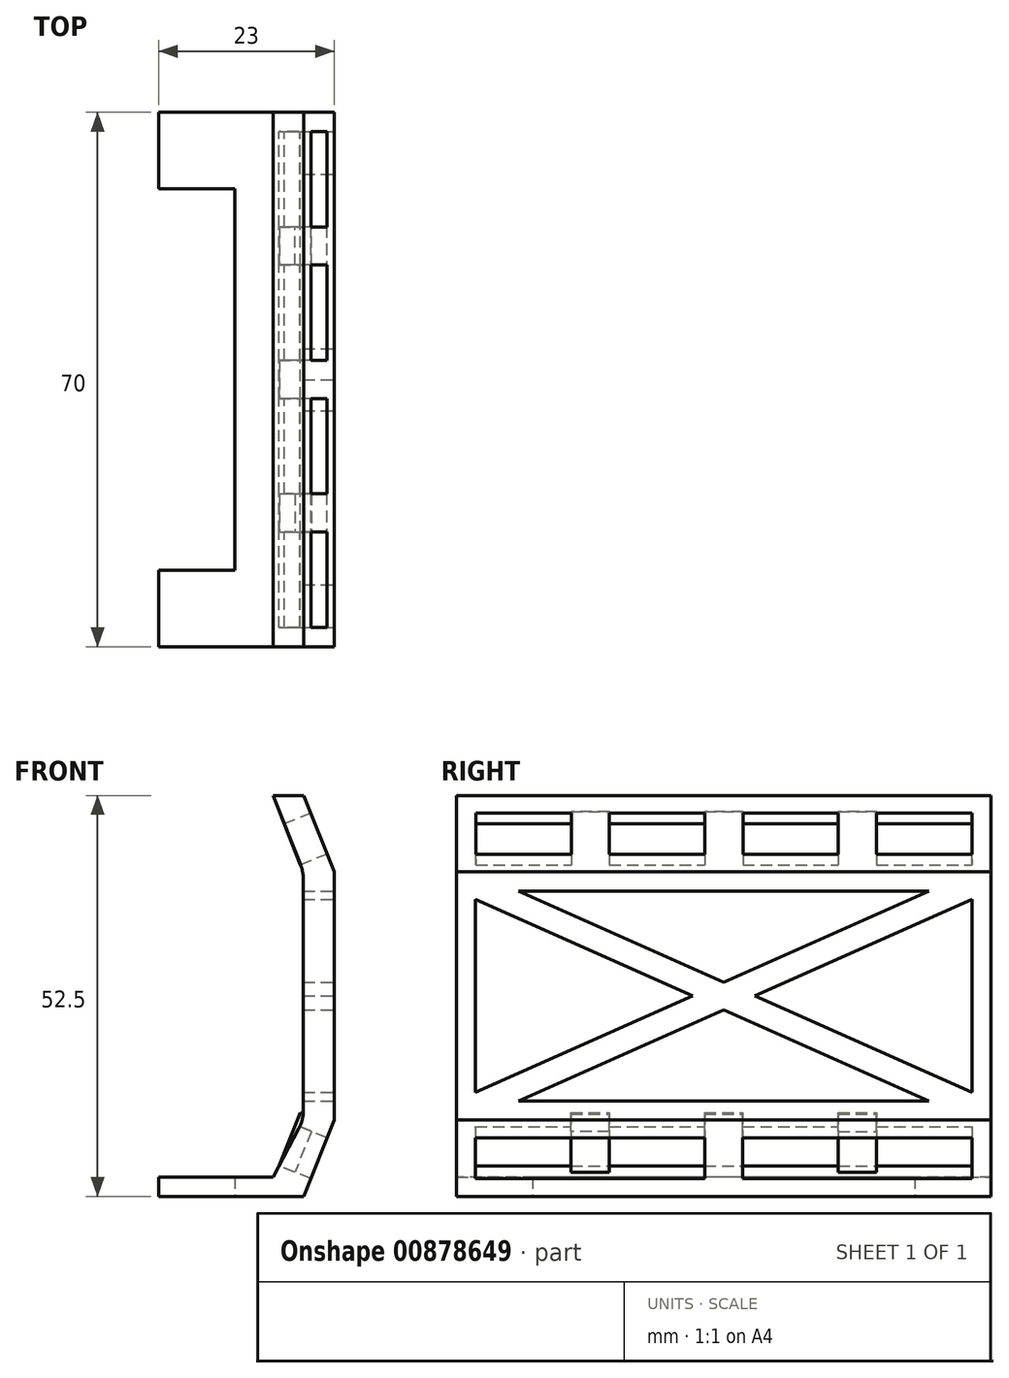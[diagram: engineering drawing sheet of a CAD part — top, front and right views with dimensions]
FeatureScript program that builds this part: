
annotation { "Feature Type Name" : "Feature", "Feature Type Description" : "" }
export const myFeature = defineFeature(function(context is Context, id is Id, definition is map)
    precondition{}
    {
        {
            var Q0;
            Q0=qCreatedBy(makeId("Top.planeOp"),FACE);
            var sketch = newSketch(context, id + "F0", { "sketchPlane" : qUnion([Q0])});
            skLineSegment(sketch, "E0.bottom", {"start": v(10, -35) * mm, "end": v(-10, -35) * mm});
            skLineSegment(sketch, "E0.top", {"start": v(10, 35) * mm, "end": v(-10, 35) * mm});
            skLineSegment(sketch, "E0.left", {"start": v(10, -35) * mm, "end": v(10, 35) * mm});
            skLineSegment(sketch, "E0.right", {"start": v(-10, -35) * mm, "end": v(-10, 35) * mm});
            skPoint(sketch, "E0.middle", {"position": v(0, 0) * mm});
            skLineSegment(sketch, "E1", {"start": v(-10, -35) * mm, "end": v(-10, -25) * mm});
            skLineSegment(sketch, "E2", {"start": v(-10, 35) * mm, "end": v(-10, 25) * mm});
            skLineSegment(sketch, "E3.bottom", {"start": v(-10, 25) * mm, "end": v(0, 25) * mm});
            skLineSegment(sketch, "E3.top", {"start": v(-10, -25) * mm, "end": v(0, -25) * mm});
            skLineSegment(sketch, "E3.left", {"start": v(-10, 25) * mm, "end": v(-10, -25) * mm});
            skLineSegment(sketch, "E3.right", {"start": v(0, 25) * mm, "end": v(0, -25) * mm});
            skSolve(sketch);
        }
        {
            var Q0;
            Q0=makeQuery(id+"F0.imprint","IMPRINT",FACE,{"disambiguationData":[TD([[makeQuery(id+"F0.imprint","IMPRINT",EDGE,{"derivedFrom":sQuery(id+"F0.wireOp",EDGE,"E0.bottom")}),-1.0]])]});
            extrude(context, id + "F1", {"entities" : qUnion([Q0]), "depth" : 2.5 * mm, "offsetDistance" : 25 * mm});
        }
        {
            var Q0;
            Q0=makeQuery(id+"F1.opExtrude","CAP_FACE",FACE,{"disambiguationData":[OSD([sQuery(id+"F0.wireOp",EDGE,"E0.bottom"),sQuery(id+"F0.wireOp",EDGE,"E0.top"),sQuery(id+"F0.wireOp",EDGE,"E0.left"),sQuery(id+"F0.wireOp",EDGE,"E1"),sQuery(id+"F0.wireOp",EDGE,"E2"),sQuery(id+"F0.wireOp",EDGE,"E3.bottom"),sQuery(id+"F0.wireOp",EDGE,"E3.top"),sQuery(id+"F0.wireOp",EDGE,"E3.right")])],"isStart":false});
            var sketch = newSketch(context, id + "F2", { "sketchPlane" : qUnion([Q0])});
            skLineSegment(sketch, "E4.bottom", {"start": v(10, 35) * mm, "end": v(5, 35) * mm});
            skLineSegment(sketch, "E4.top", {"start": v(10, -35) * mm, "end": v(5, -35) * mm});
            skLineSegment(sketch, "E4.left", {"start": v(10, 35) * mm, "end": v(10, -35) * mm});
            skLineSegment(sketch, "E4.right", {"start": v(5, 35) * mm, "end": v(5, -35) * mm});
            skSolve(sketch);
        }
        {
            var Q0;
            Q0=makeQuery(id+"F2.imprint","IMPRINT",FACE,{"disambiguationData":[TD([[makeQuery(id+"F2.imprint","IMPRINT",EDGE,{"derivedFrom":sQuery(id+"F2.wireOp",EDGE,"E4.bottom")}),1.0]])]});
            extrude(context, id + "F3", {"entities" : qUnion([Q0]), "operationType" : NewBodyOperationType.ADD, "depth" : 50 * mm, "offsetDistance" : 25 * mm});
        }
        {
            var Q0;
            Q0=makeQuery(id+"F3.boolean.opBoolean","MERGE",FACE,{"derivedFrom":[makeQuery(id+"F1.opExtrude","SWEPT_FACE",FACE,{"disambiguationData":[OSD([sQuery(id+"F0.wireOp",EDGE,"E0.left")])]}),makeQuery(id+"F3.opExtrude","SWEPT_FACE",FACE,{"disambiguationData":[OSD([sQuery(id+"F2.wireOp",EDGE,"E4.left")])]})]});
            extrude(context, id + "F4", {"entities" : qUnion([Q0]), "operationType" : NewBodyOperationType.ADD, "depth" : 3 * mm, "offsetDistance" : 25 * mm});
        }
        {
            var Q0;
            {var subQ0=sQuery(id+"F2.wireOp",EDGE,"E4.top");var subQ1=sQuery(id+"F0.wireOp",EDGE,"E0.bottom");Q0=makeQuery(id+"F4.boolean.opBoolean","MERGE",FACE,{"derivedFrom":[makeQuery(id+"F3.boolean.opBoolean","MERGE",FACE,{"derivedFrom":[makeQuery(id+"F1.opExtrude","SWEPT_FACE",FACE,{"disambiguationData":[OSD([subQ1])]}),makeQuery(id+"F3.opExtrude","SWEPT_FACE",FACE,{"disambiguationData":[OSD([subQ0])]})]}),makeQuery(id+"F4.opExtrude","SWEPT_FACE",FACE,{"disambiguationData":[OSD([subQ1,sQuery(id+"F0.wireOp",EDGE,"E0.left"),subQ0,sQuery(id+"F2.wireOp",EDGE,"E4.left")])]})]});}
            var sketch = newSketch(context, id + "F5", { "sketchPlane" : qUnion([Q0])});
            skLineSegment(sketch, "E5", {"start": v(13, 52.5) * mm, "end": v(13, 42.5) * mm});
            skLineSegment(sketch, "E6", {"start": v(13, 0) * mm, "end": v(13, 10) * mm});
            skLineSegment(sketch, "E7", {"start": v(13, 42.5) * mm, "end": v(9, 52.5) * mm});
            skLineSegment(sketch, "E8", {"start": v(13, 10) * mm, "end": v(9, 0) * mm});
            skLineSegment(sketch, "E9", {"start": v(5, 2.5) * mm, "end": v(8.95, 10) * mm});
            skLineSegment(sketch, "E10", {"start": v(8.95, 10) * mm, "end": v(8.95, 42.5) * mm});
            skLineSegment(sketch, "E11", {"start": v(8.95, 42.5) * mm, "end": v(5, 52.5) * mm});
            skSolve(sketch);
        }
        {
            var Q0;
            {var subQ0=sQuery(id+"F5.wireOp",EDGE,"E6");Q0=makeQuery(id+"F5.imprint","IMPRINT",FACE,{"disambiguationData":[TD([[makeQuery(id+"F5.imprint","IMPRINT",EDGE,{"derivedFrom":subQ0}),-1.0]])]});}
            var Q1;
            Q1=makeQuery(id+"F5.imprint","IMPRINT",FACE,{"disambiguationData":[TD([[makeQuery(id+"F5.imprint","IMPRINT",EDGE,{"derivedFrom":sQuery(id+"F5.wireOp",EDGE,"E9")}),1.0]])]});
            var Q2;
            {var subQ0=sQuery(id+"F5.wireOp",EDGE,"E5");Q2=makeQuery(id+"F5.imprint","IMPRINT",FACE,{"disambiguationData":[TD([[makeQuery(id+"F5.imprint","IMPRINT",EDGE,{"derivedFrom":subQ0}),-1.0]])]});}
            extrude(context, id + "F6", {"entities" : qUnion([Q0, Q1, Q2]), "operationType" : NewBodyOperationType.REMOVE, "oppositeDirection" : true, "depth" : 70 * mm, "offsetDistance" : 25 * mm});
        }
        {
            var Q0;
            Q0=makeQuery(id+"F6.boolean.opBoolean","COPY",FACE,{"derivedFrom":makeQuery(id+"F6.opExtrude","SWEPT_FACE",FACE,{"disambiguationData":[OSD([sQuery(id+"F5.wireOp",EDGE,"E7")])]})});
            var sketch = newSketch(context, id + "F7", { "sketchPlane" : qUnion([Q0])});
            skLineSegment(sketch, "E12.bottom", {"start": v(-32.45, 42.9) * mm, "end": v(32.5, 42.9) * mm});
            skLineSegment(sketch, "E12.top", {"start": v(-32.45, 37.13) * mm, "end": v(32.5, 37.13) * mm});
            skLineSegment(sketch, "E12.left", {"start": v(-32.45, 42.9) * mm, "end": v(-32.45, 37.13) * mm});
            skLineSegment(sketch, "E12.right", {"start": v(32.5, 42.9) * mm, "end": v(32.5, 37.13) * mm});
            skPoint(sketch, "E13.end.orphan", {"position": v(35, 37.13) * mm});
            skPoint(sketch, "E14.end.orphan", {"position": v(-32.45, 45.4) * mm});
            skSolve(sketch);
        }
        {
            var Q0;
            Q0=makeQuery(id+"F7.imprint","IMPRINT",FACE,{"disambiguationData":[TD([[makeQuery(id+"F7.imprint","IMPRINT",EDGE,{"derivedFrom":sQuery(id+"F7.wireOp",EDGE,"E12.bottom")}),-1.0]])]});
            extrude(context, id + "F8", {"entities" : qUnion([Q0]), "operationType" : NewBodyOperationType.REMOVE, "oppositeDirection" : true, "depth" : 25 * mm, "offsetDistance" : 25 * mm});
        }
        {
            var Q0;
            Q0=makeQuery(id+"F4.opExtrude","CAP_FACE",FACE,{"disambiguationData":[OSD([sQuery(id+"F0.wireOp",EDGE,"E0.left"),sQuery(id+"F2.wireOp",EDGE,"E4.left")])],"isStart":false});
            var sketch = newSketch(context, id + "F9", { "sketchPlane" : qUnion([Q0])});
            skLineSegment(sketch, "E15", {"start": v(35, 10) * mm, "end": v(35, 12.5) * mm});
            skLineSegment(sketch, "E16", {"start": v(35, 10) * mm, "end": v(32.5, 10) * mm});
            skLineSegment(sketch, "E17", {"start": v(32.5, 10) * mm, "end": v(32.5, 12.5) * mm});
            skLineSegment(sketch, "E18", {"start": v(32.5, 12.5) * mm, "end": v(35, 12.5) * mm});
            skLineSegment(sketch, "E19", {"start": v(-32.5, 42.5) * mm, "end": v(-32.5, 40) * mm});
            skLineSegment(sketch, "E20", {"start": v(-32.5, 40) * mm, "end": v(-35, 40) * mm});
            skLineSegment(sketch, "E21.bottom", {"start": v(32.5, 12.5) * mm, "end": v(-32.5, 12.5) * mm});
            skLineSegment(sketch, "E21.top", {"start": v(32.5, 40) * mm, "end": v(-32.5, 40) * mm});
            skLineSegment(sketch, "E21.left", {"start": v(32.5, 12.5) * mm, "end": v(32.5, 40) * mm});
            skLineSegment(sketch, "E21.right", {"start": v(-32.5, 12.5) * mm, "end": v(-32.5, 40) * mm});
            skLineSegment(sketch, "E22", {"start": v(-32.5, 42.5) * mm, "end": v(35, 12.5) * mm});
            skLineSegment(sketch, "E23", {"start": v(32.5, 10) * mm, "end": v(-35, 40) * mm});
            skLineSegment(sketch, "E24.bottom", {"start": v(32.5, 40) * mm, "end": v(35, 40) * mm});
            skLineSegment(sketch, "E24.top", {"start": v(32.5, 42.5) * mm, "end": v(35, 42.5) * mm});
            skLineSegment(sketch, "E24.left", {"start": v(32.5, 40) * mm, "end": v(32.5, 42.5) * mm});
            skLineSegment(sketch, "E24.right", {"start": v(35, 40) * mm, "end": v(35, 42.5) * mm});
            skLineSegment(sketch, "E25.bottom", {"start": v(-32.5, 12.5) * mm, "end": v(-35, 12.5) * mm});
            skLineSegment(sketch, "E25.top", {"start": v(-32.5, 10) * mm, "end": v(-35, 10) * mm});
            skLineSegment(sketch, "E25.left", {"start": v(-32.5, 12.5) * mm, "end": v(-32.5, 10) * mm});
            skLineSegment(sketch, "E25.right", {"start": v(-35, 12.5) * mm, "end": v(-35, 10) * mm});
            skLineSegment(sketch, "E26", {"start": v(-35, 12.5) * mm, "end": v(32.5, 42.5) * mm});
            skLineSegment(sketch, "E27", {"start": v(-32.5, 10) * mm, "end": v(35, 40) * mm});
            skSolve(sketch);
        }
        {
            var Q0;
            Q0=makeQuery(id+"F9.imprint","IMPRINT",FACE,{"disambiguationData":[TD([[makeQuery(id+"F9.imprint","IMPRINT",EDGE,{"derivedFrom":sQuery(id+"F9.wireOp",EDGE,"E21.bottom")}),-1.0]])]});
            var Q1;
            {var subQ0=sQuery(id+"F9.wireOp",EDGE,"E26");var subQ1=sQuery(id+"F9.wireOp",EDGE,"E21.right");var subQ2=makeQuery(id+"F9.imprint","INTERSECT",VERTEX,{"derivedFrom":[subQ1,subQ0]});Q1=makeQuery(id+"F9.imprint","IMPRINT",FACE,{"disambiguationData":[TD([[makeQuery(id+"F9.imprint","IMPRINT",EDGE,{"disambiguationData":[TD([[subQ2,-1.0]])],"derivedFrom":subQ1}),-1.0]])]});}
            var Q2;
            {var subQ0=sQuery(id+"F9.wireOp",EDGE,"E26");var subQ1=sQuery(id+"F9.wireOp",EDGE,"E21.top");var subQ2=makeQuery(id+"F9.imprint","INTERSECT",VERTEX,{"derivedFrom":[subQ1,subQ0]});Q2=makeQuery(id+"F9.imprint","IMPRINT",FACE,{"disambiguationData":[TD([[makeQuery(id+"F9.imprint","IMPRINT",EDGE,{"disambiguationData":[TD([[subQ2,-1.0]])],"derivedFrom":subQ1}),1.0]])]});}
            var Q3;
            {var subQ0=sQuery(id+"F9.wireOp",EDGE,"E22");var subQ1=sQuery(id+"F9.wireOp",EDGE,"E21.left");var subQ2=makeQuery(id+"F9.imprint","INTERSECT",VERTEX,{"derivedFrom":[subQ1,subQ0]});Q3=makeQuery(id+"F9.imprint","IMPRINT",FACE,{"disambiguationData":[TD([[makeQuery(id+"F9.imprint","IMPRINT",EDGE,{"disambiguationData":[TD([[subQ2,-1.0]])],"derivedFrom":subQ1}),1.0]])]});}
            extrude(context, id + "F10", {"entities" : qUnion([Q0, Q1, Q2, Q3]), "operationType" : NewBodyOperationType.REMOVE, "oppositeDirection" : true, "depth" : 25 * mm, "offsetDistance" : 25 * mm});
        }
        {
            var Q0;
            Q0=makeQuery(id+"F6.boolean.opBoolean","COPY",FACE,{"derivedFrom":makeQuery(id+"F6.opExtrude","SWEPT_FACE",FACE,{"disambiguationData":[OSD([sQuery(id+"F5.wireOp",EDGE,"E8")])]})});
            var sketch = newSketch(context, id + "F11", { "sketchPlane" : qUnion([Q0])});
            skLineSegment(sketch, "E28", {"start": v(-32.5, 14.11) * mm, "end": v(-32.5, 11.61) * mm});
            skLineSegment(sketch, "E29", {"start": v(-32.5, 11.61) * mm, "end": v(-35, 11.61) * mm});
            skLineSegment(sketch, "E30", {"start": v(35, 5.84) * mm, "end": v(32.5, 5.84) * mm});
            skLineSegment(sketch, "E31", {"start": v(32.5, 5.84) * mm, "end": v(32.5, 3.34) * mm});
            skLineSegment(sketch, "E32.bottom", {"start": v(-32.5, 11.61) * mm, "end": v(32.5, 11.61) * mm});
            skLineSegment(sketch, "E32.top", {"start": v(-32.5, 5.84) * mm, "end": v(32.5, 5.84) * mm});
            skLineSegment(sketch, "E32.left", {"start": v(-32.5, 11.61) * mm, "end": v(-32.5, 5.84) * mm});
            skLineSegment(sketch, "E32.right", {"start": v(32.5, 11.61) * mm, "end": v(32.5, 5.84) * mm});
            skSolve(sketch);
        }
        {
            var Q0;
            Q0=makeQuery(id+"F11.imprint","IMPRINT",FACE,{"disambiguationData":[TD([[makeQuery(id+"F11.imprint","IMPRINT",EDGE,{"derivedFrom":sQuery(id+"F11.wireOp",EDGE,"E32.bottom")}),-1.0]])]});
            extrude(context, id + "F12", {"entities" : qUnion([Q0]), "operationType" : NewBodyOperationType.REMOVE, "oppositeDirection" : true, "depth" : 25 * mm, "offsetDistance" : 25 * mm});
        }
        {
            var Q0;
            Q0=makeQuery(id+"F6.boolean.opBoolean","COPY",EDGE,{"derivedFrom":makeQuery(id+"F6.opExtrude","SWEPT_EDGE",EDGE,{"disambiguationData":[OSD([sQuery(id+"F0.wireOp",EDGE,"E0.bottom"),sQuery(id+"F0.wireOp",EDGE,"E0.left"),sQuery(id+"F2.wireOp",EDGE,"E4.top"),sQuery(id+"F2.wireOp",EDGE,"E4.left"),sQuery(id+"F5.wireOp",EDGE,"E6"),sQuery(id+"F5.wireOp",EDGE,"E8")])]})});
            var Q1;
            Q1=makeQuery(id+"F6.boolean.opBoolean","COPY",EDGE,{"derivedFrom":makeQuery(id+"F6.opExtrude","SWEPT_EDGE",EDGE,{"disambiguationData":[OSD([sQuery(id+"F0.wireOp",EDGE,"E0.bottom"),sQuery(id+"F0.wireOp",EDGE,"E0.left"),sQuery(id+"F2.wireOp",EDGE,"E4.top"),sQuery(id+"F2.wireOp",EDGE,"E4.left"),sQuery(id+"F5.wireOp",EDGE,"E5"),sQuery(id+"F5.wireOp",EDGE,"E7")])]})});
            var Q2;
            Q2=makeQuery(id+"F6.boolean.opBoolean","COPY",EDGE,{"derivedFrom":makeQuery(id+"F6.opExtrude","SWEPT_EDGE",EDGE,{"disambiguationData":[OSD([sQuery(id+"F5.wireOp",EDGE,"E9"),sQuery(id+"F5.wireOp",EDGE,"E10")])]})});
            var Q3;
            Q3=makeQuery(id+"F6.boolean.opBoolean","COPY",EDGE,{"derivedFrom":makeQuery(id+"F6.opExtrude","SWEPT_EDGE",EDGE,{"disambiguationData":[OSD([sQuery(id+"F5.wireOp",EDGE,"E10"),sQuery(id+"F5.wireOp",EDGE,"E11")])]})});
            fillet(context, id + "F13", {"entities" : qUnion([Q0, Q1, Q2, Q3]), "radius" : 5 * mm, "tangentPropagation" : true, "allowEdgeOverflow" : false});
        }
        {
            var Q0;
            Q0=makeQuery(id+"F12.boolean.opBoolean","COPY",FACE,{"derivedFrom":makeQuery(id+"F12.opExtrude","SWEPT_FACE",FACE,{"disambiguationData":[OSD([sQuery(id+"F11.wireOp",EDGE,"E32.top")])]})});
            var sketch = newSketch(context, id + "F14", { "sketchPlane" : qUnion([Q0])});
            skLineSegment(sketch, "E33", {"start": v(8.36, -32.5) * mm, "end": v(8.36, 32.5) * mm});
            skLineSegment(sketch, "E34", {"start": v(8.36, 0) * mm, "end": v(3.89, 0) * mm});
            skLineSegment(sketch, "E35", {"start": v(3.89, 0) * mm, "end": v(6.12, 0) * mm});
            skLineSegment(sketch, "E36", {"start": v(6.12, 0) * mm, "end": v(6.12, 2.5) * mm});
            skLineSegment(sketch, "E37", {"start": v(6.12, 0) * mm, "end": v(6.12, -2.5) * mm});
            skLineSegment(sketch, "E38.bottom", {"start": v(8.36, 2.5) * mm, "end": v(3.89, 2.5) * mm});
            skLineSegment(sketch, "E38.top", {"start": v(8.36, -2.5) * mm, "end": v(3.89, -2.5) * mm});
            skLineSegment(sketch, "E38.left", {"start": v(8.36, 2.5) * mm, "end": v(8.36, -2.5) * mm});
            skLineSegment(sketch, "E38.right", {"start": v(3.89, 2.5) * mm, "end": v(3.89, -2.5) * mm});
            skPoint(sketch, "E38.middle", {"position": v(6.12, 0) * mm});
            skLineSegment(sketch, "E39", {"start": v(6.12, 2.5) * mm, "end": v(6.12, 32.5) * mm});
            skLineSegment(sketch, "E40", {"start": v(6.12, -2.5) * mm, "end": v(6.12, -32.5) * mm});
            skLineSegment(sketch, "E41", {"start": v(6.12, -2.5) * mm, "end": v(6.12, -17.5) * mm});
            skLineSegment(sketch, "E42", {"start": v(6.12, -17.5) * mm, "end": v(6.12, 17.5) * mm});
            skLineSegment(sketch, "E43.bottom", {"start": v(8.36, -15) * mm, "end": v(3.89, -15) * mm});
            skLineSegment(sketch, "E43.top", {"start": v(8.36, -20) * mm, "end": v(3.89, -20) * mm});
            skLineSegment(sketch, "E43.left", {"start": v(8.36, -15) * mm, "end": v(8.36, -20) * mm});
            skLineSegment(sketch, "E43.right", {"start": v(3.89, -15) * mm, "end": v(3.89, -20) * mm});
            skPoint(sketch, "E43.middle", {"position": v(6.12, -17.5) * mm});
            skLineSegment(sketch, "E44.bottom", {"start": v(8.36, 20) * mm, "end": v(3.89, 20) * mm});
            skLineSegment(sketch, "E44.top", {"start": v(8.36, 15) * mm, "end": v(3.89, 15) * mm});
            skLineSegment(sketch, "E44.left", {"start": v(8.36, 20) * mm, "end": v(8.36, 15) * mm});
            skLineSegment(sketch, "E44.right", {"start": v(3.89, 20) * mm, "end": v(3.89, 15) * mm});
            skPoint(sketch, "E44.middle", {"position": v(6.12, 17.5) * mm});
            skSolve(sketch);
        }
        {
            var Q0;
            {var subQ0=sQuery(id+"F14.wireOp",EDGE,"E35");Q0=makeQuery(id+"F14.imprint","IMPRINT",FACE,{"disambiguationData":[TD([[makeQuery(id+"F14.imprint","IMPRINT",EDGE,{"derivedFrom":subQ0}),1.0]])]});}
            var Q1;
            {var subQ0=sQuery(id+"F14.wireOp",EDGE,"E35");Q1=makeQuery(id+"F14.imprint","IMPRINT",FACE,{"disambiguationData":[TD([[makeQuery(id+"F14.imprint","IMPRINT",EDGE,{"derivedFrom":subQ0}),-1.0]])]});}
            var Q2;
            {var subQ0=sQuery(id+"F14.wireOp",EDGE,"E34");Q2=makeQuery(id+"F14.imprint","IMPRINT",FACE,{"disambiguationData":[TD([[makeQuery(id+"F14.imprint","IMPRINT",EDGE,{"derivedFrom":subQ0}),1.0]])]});}
            var Q3;
            {var subQ0=sQuery(id+"F14.wireOp",EDGE,"E34");Q3=makeQuery(id+"F14.imprint","IMPRINT",FACE,{"disambiguationData":[TD([[makeQuery(id+"F14.imprint","IMPRINT",EDGE,{"derivedFrom":subQ0}),-1.0]])]});}
            var Q4;
            {var subQ0=sQuery(id+"F14.wireOp",EDGE,"E43.left");Q4=makeQuery(id+"F14.imprint","IMPRINT",FACE,{"disambiguationData":[TD([[makeQuery(id+"F14.imprint","IMPRINT",EDGE,{"derivedFrom":subQ0}),1.0]])]});}
            var Q5;
            {var subQ0=sQuery(id+"F14.wireOp",EDGE,"E43.right");Q5=makeQuery(id+"F14.imprint","IMPRINT",FACE,{"disambiguationData":[TD([[makeQuery(id+"F14.imprint","IMPRINT",EDGE,{"derivedFrom":subQ0}),-1.0]])]});}
            var Q6;
            {var subQ0=sQuery(id+"F14.wireOp",EDGE,"E44.right");Q6=makeQuery(id+"F14.imprint","IMPRINT",FACE,{"disambiguationData":[TD([[makeQuery(id+"F14.imprint","IMPRINT",EDGE,{"derivedFrom":subQ0}),-1.0]])]});}
            var Q7;
            {var subQ0=sQuery(id+"F14.wireOp",EDGE,"E44.left");Q7=makeQuery(id+"F14.imprint","IMPRINT",FACE,{"disambiguationData":[TD([[makeQuery(id+"F14.imprint","IMPRINT",EDGE,{"derivedFrom":subQ0}),1.0]])]});}
            extrude(context, id + "F15", {"entities" : qUnion([Q0, Q1, Q2, Q3, Q4, Q5, Q6, Q7]), "operationType" : NewBodyOperationType.ADD, "depth" : 7.5 * mm, "offsetDistance" : 25 * mm});
        }
        {
            var Q0;
            Q0=makeQuery(id+"F8.boolean.opBoolean","COPY",FACE,{"derivedFrom":makeQuery(id+"F8.opExtrude","SWEPT_FACE",FACE,{"disambiguationData":[OSD([sQuery(id+"F7.wireOp",EDGE,"E12.top")])]})});
            var sketch = newSketch(context, id + "F16", { "sketchPlane" : qUnion([Q0])});
            skLineSegment(sketch, "E45", {"start": v(24.1, 0.02) * mm, "end": v(27.85, 0) * mm});
            skLineSegment(sketch, "E46", {"start": v(25.98, 0.01) * mm, "end": v(25.98, 2.51) * mm});
            skLineSegment(sketch, "E47", {"start": v(25.98, 0.01) * mm, "end": v(25.98, -2.49) * mm});
            skLineSegment(sketch, "E48.bottom", {"start": v(27.85, 2.51) * mm, "end": v(24.1, 2.51) * mm});
            skLineSegment(sketch, "E48.top", {"start": v(27.85, -2.49) * mm, "end": v(24.1, -2.49) * mm});
            skLineSegment(sketch, "E48.left", {"start": v(27.85, 2.51) * mm, "end": v(27.85, -2.49) * mm});
            skLineSegment(sketch, "E48.right", {"start": v(24.1, 2.51) * mm, "end": v(24.1, -2.49) * mm});
            skPoint(sketch, "E48.middle", {"position": v(25.98, 0.01) * mm});
            skLineSegment(sketch, "E49", {"start": v(25.98, -2.49) * mm, "end": v(25.98, -32.45) * mm});
            skLineSegment(sketch, "E50", {"start": v(25.98, 2.51) * mm, "end": v(25.98, 32.5) * mm});
            skLineSegment(sketch, "E51", {"start": v(25.98, 32.5) * mm, "end": v(25.98, 17.5) * mm});
            skLineSegment(sketch, "E52", {"start": v(25.98, 17.5) * mm, "end": v(25.98, -17.47) * mm});
            skLineSegment(sketch, "E53.bottom", {"start": v(27.85, -14.97) * mm, "end": v(24.1, -14.97) * mm});
            skLineSegment(sketch, "E53.top", {"start": v(27.85, -19.97) * mm, "end": v(24.1, -19.97) * mm});
            skLineSegment(sketch, "E53.left", {"start": v(27.85, -14.97) * mm, "end": v(27.85, -19.97) * mm});
            skLineSegment(sketch, "E53.right", {"start": v(24.1, -14.97) * mm, "end": v(24.1, -19.97) * mm});
            skPoint(sketch, "E53.middle", {"position": v(25.98, -17.47) * mm});
            skLineSegment(sketch, "E54.bottom", {"start": v(27.85, 20) * mm, "end": v(24.1, 20) * mm});
            skLineSegment(sketch, "E54.top", {"start": v(27.85, 15) * mm, "end": v(24.1, 15) * mm});
            skLineSegment(sketch, "E54.left", {"start": v(27.85, 20) * mm, "end": v(27.85, 15) * mm});
            skLineSegment(sketch, "E54.right", {"start": v(24.1, 20) * mm, "end": v(24.1, 15) * mm});
            skPoint(sketch, "E54.middle", {"position": v(25.98, 17.5) * mm});
            skSolve(sketch);
        }
        {
            var Q0;
            {var subQ0=sQuery(id+"F16.wireOp",EDGE,"E53.right");Q0=makeQuery(id+"F16.imprint","IMPRINT",FACE,{"disambiguationData":[TD([[makeQuery(id+"F16.imprint","IMPRINT",EDGE,{"derivedFrom":subQ0}),-1.0]])]});}
            var Q1;
            {var subQ0=sQuery(id+"F16.wireOp",EDGE,"E53.left");Q1=makeQuery(id+"F16.imprint","IMPRINT",FACE,{"disambiguationData":[TD([[makeQuery(id+"F16.imprint","IMPRINT",EDGE,{"derivedFrom":subQ0}),1.0]])]});}
            var Q2;
            {var subQ0=sQuery(id+"F16.wireOp",EDGE,"E48.right");var subQ1=sQuery(id+"F16.wireOp",EDGE,"E45");var subQ2=makeQuery(id+"F16.imprint","INTERSECT",VERTEX,{"derivedFrom":[subQ1,subQ0]});Q2=makeQuery(id+"F16.imprint","IMPRINT",FACE,{"disambiguationData":[TD([[makeQuery(id+"F16.imprint","IMPRINT",EDGE,{"disambiguationData":[TD([[subQ2,-1.0]])],"derivedFrom":subQ1}),1.0]])]});}
            var Q3;
            {var subQ0=sQuery(id+"F16.wireOp",EDGE,"E48.right");var subQ1=sQuery(id+"F16.wireOp",EDGE,"E45");var subQ2=makeQuery(id+"F16.imprint","INTERSECT",VERTEX,{"derivedFrom":[subQ1,subQ0]});Q3=makeQuery(id+"F16.imprint","IMPRINT",FACE,{"disambiguationData":[TD([[makeQuery(id+"F16.imprint","IMPRINT",EDGE,{"disambiguationData":[TD([[subQ2,-1.0]])],"derivedFrom":subQ1}),-1.0]])]});}
            var Q4;
            {var subQ0=sQuery(id+"F16.wireOp",EDGE,"E48.left");var subQ1=sQuery(id+"F16.wireOp",EDGE,"E45");var subQ2=makeQuery(id+"F16.imprint","INTERSECT",VERTEX,{"derivedFrom":[subQ1,subQ0]});Q4=makeQuery(id+"F16.imprint","IMPRINT",FACE,{"disambiguationData":[TD([[makeQuery(id+"F16.imprint","IMPRINT",EDGE,{"disambiguationData":[TD([[subQ2,1.0]])],"derivedFrom":subQ1}),-1.0]])]});}
            var Q5;
            {var subQ0=sQuery(id+"F16.wireOp",EDGE,"E48.left");var subQ1=sQuery(id+"F16.wireOp",EDGE,"E45");var subQ2=makeQuery(id+"F16.imprint","INTERSECT",VERTEX,{"derivedFrom":[subQ1,subQ0]});Q5=makeQuery(id+"F16.imprint","IMPRINT",FACE,{"disambiguationData":[TD([[makeQuery(id+"F16.imprint","IMPRINT",EDGE,{"disambiguationData":[TD([[subQ2,1.0]])],"derivedFrom":subQ1}),1.0]])]});}
            var Q6;
            {var subQ0=sQuery(id+"F16.wireOp",EDGE,"E54.left");Q6=makeQuery(id+"F16.imprint","IMPRINT",FACE,{"disambiguationData":[TD([[makeQuery(id+"F16.imprint","IMPRINT",EDGE,{"derivedFrom":subQ0}),1.0]])]});}
            var Q7;
            {var subQ0=sQuery(id+"F16.wireOp",EDGE,"E54.right");Q7=makeQuery(id+"F16.imprint","IMPRINT",FACE,{"disambiguationData":[TD([[makeQuery(id+"F16.imprint","IMPRINT",EDGE,{"derivedFrom":subQ0}),-1.0]])]});}
            extrude(context, id + "F17", {"entities" : qUnion([Q0, Q1, Q2, Q3, Q4, Q5, Q6, Q7]), "operationType" : NewBodyOperationType.ADD, "depth" : 7.5 * mm, "offsetDistance" : 25 * mm});
        }
    });
